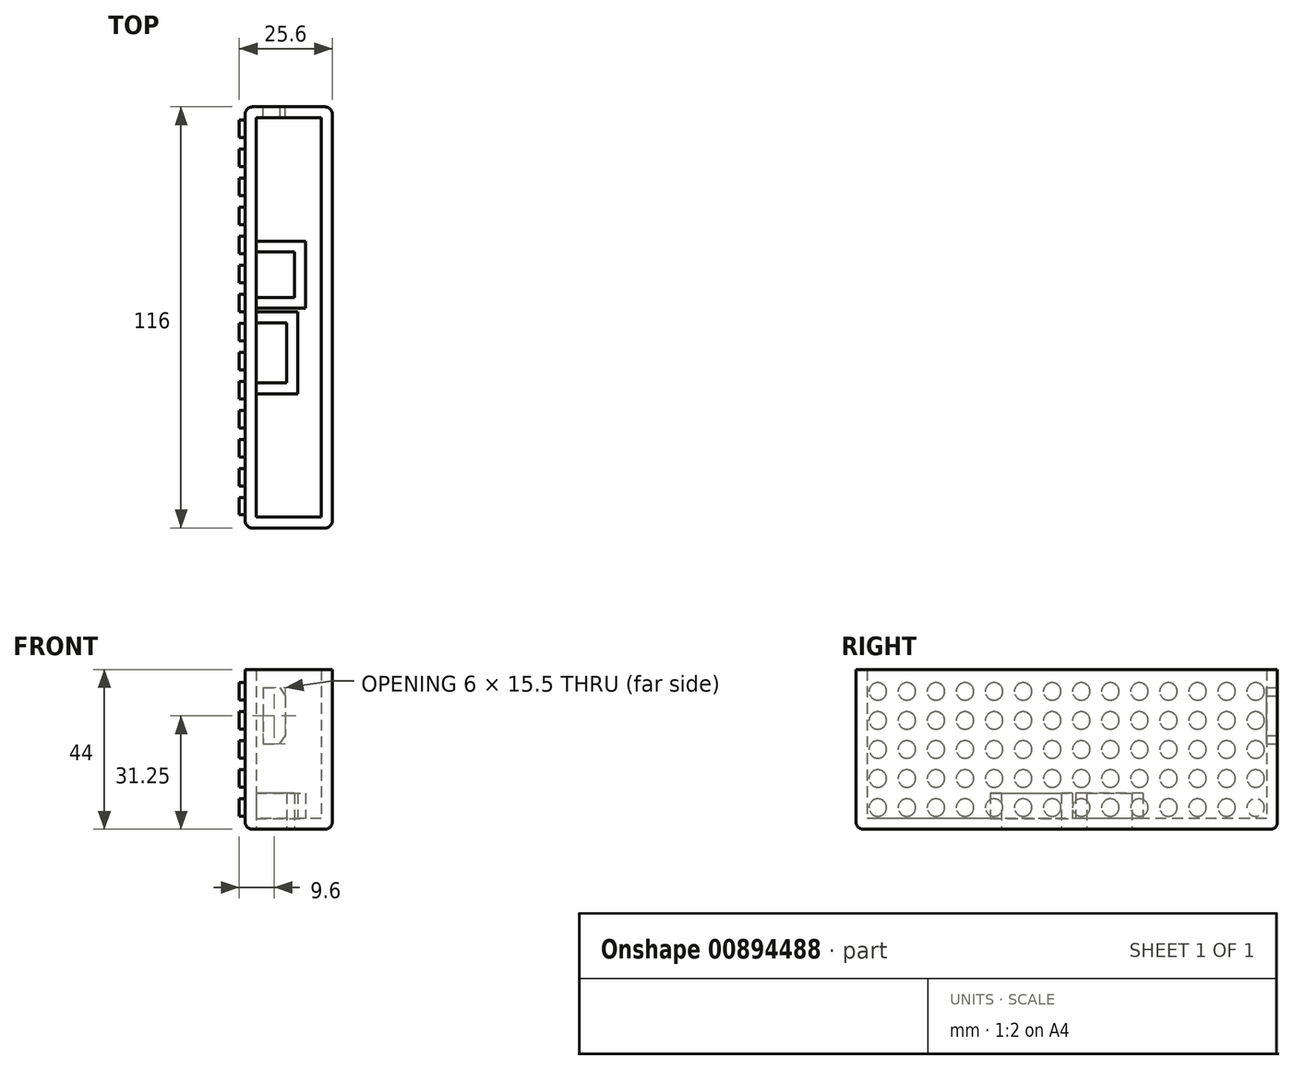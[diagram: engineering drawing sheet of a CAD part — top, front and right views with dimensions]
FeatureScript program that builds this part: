
annotation { "Feature Type Name" : "Feature", "Feature Type Description" : "" }
export const myFeature = defineFeature(function(context is Context, id is Id, definition is map)
    precondition{}
    {
        {
            var Q0;
            Q0=qCreatedBy(makeId("Top.planeOp"),FACE);
            var sketch = newSketch(context, id + "F0", { "sketchPlane" : qUnion([Q0])});
            skLineSegment(sketch, "E0.bottom", {"start": v(12, 58) * mm, "end": v(-12, 58) * mm});
            skLineSegment(sketch, "E0.top", {"start": v(12, -58) * mm, "end": v(-12, -58) * mm});
            skLineSegment(sketch, "E0.left", {"start": v(12, 58) * mm, "end": v(12, -58) * mm});
            skLineSegment(sketch, "E0.right", {"start": v(-12, 58) * mm, "end": v(-12, -58) * mm});
            skPoint(sketch, "E0.middle", {"position": v(0, 0) * mm});
            skSolve(sketch);
        }
        {
            var Q0;
            Q0=makeQuery(id+"F0.imprint","IMPRINT",FACE,{"disambiguationData":[TD([[makeQuery(id+"F0.imprint","IMPRINT",EDGE,{"derivedFrom":sQuery(id+"F0.wireOp",EDGE,"E0.bottom")}),1.0]])]});
            extrude(context, id + "F1", {"entities" : qUnion([Q0]), "depth" : 44 * mm, "offsetDistance" : 25 * mm});
        }
        {
            var Q0;
            Q0=makeQuery(id+"F1.opExtrude","CAP_FACE",FACE,{"disambiguationData":[OSD([sQuery(id+"F0.wireOp",EDGE,"E0.bottom"),sQuery(id+"F0.wireOp",EDGE,"E0.top"),sQuery(id+"F0.wireOp",EDGE,"E0.left"),sQuery(id+"F0.wireOp",EDGE,"E0.right")])],"isStart":false});
            shell(context, id + "F2", {"entities" : qUnion([Q0]), "thickness" : 3 * mm});
        }
        {
            var Q0;
            Q0=makeQuery(id+"F1.opExtrude","CAP_FACE",FACE,{"disambiguationData":[OSD([sQuery(id+"F0.wireOp",EDGE,"E0.bottom"),sQuery(id+"F0.wireOp",EDGE,"E0.top"),sQuery(id+"F0.wireOp",EDGE,"E0.left"),sQuery(id+"F0.wireOp",EDGE,"E0.right")])],"isStart":true});
            var sketch = newSketch(context, id + "F3", { "sketchPlane" : qUnion([Q0])});
            skLineSegment(sketch, "E1.bottom", {"start": v(-9, 1.5) * mm, "end": v(-0.5, 1.5) * mm});
            skLineSegment(sketch, "E1.top", {"start": v(-9, 18) * mm, "end": v(-0.5, 18) * mm});
            skLineSegment(sketch, "E1.left", {"start": v(-9, 1.5) * mm, "end": v(-9, 18) * mm});
            skLineSegment(sketch, "E1.right", {"start": v(-0.5, 1.5) * mm, "end": v(-0.5, 18) * mm});
            skLineSegment(sketch, "E2.bottom", {"start": v(-9, -18) * mm, "end": v(1.6, -18) * mm});
            skLineSegment(sketch, "E2.top", {"start": v(-9, -5.5) * mm, "end": v(1.6, -5.5) * mm});
            skLineSegment(sketch, "E2.left", {"start": v(-9, -18) * mm, "end": v(-9, -5.5) * mm});
            skLineSegment(sketch, "E2.right", {"start": v(1.6, -18) * mm, "end": v(1.6, -5.5) * mm});
            skSolve(sketch);
        }
        {
            var Q0;
            Q0 = qSketchRegion(id + "F3", true);
            extrude(context, id + "F4", {"entities" : qUnion([Q0]), "operationType" : NewBodyOperationType.REMOVE, "oppositeDirection" : true, "depth" : 25 * mm, "offsetDistance" : 25 * mm});
        }
        {
            var Q0;
            Q0=makeQuery(id+"F1.opExtrude","SWEPT_FACE",FACE,{"disambiguationData":[OSD([sQuery(id+"F0.wireOp",EDGE,"E0.bottom")])]});
            var sketch = newSketch(context, id + "F5", { "sketchPlane" : qUnion([Q0])});
            skLineSegment(sketch, "E3.bottom", {"start": v(7, 39) * mm, "end": v(1, 39) * mm});
            skLineSegment(sketch, "E3.top", {"start": v(7, 23.5) * mm, "end": v(1, 23.5) * mm});
            skLineSegment(sketch, "E3.left", {"start": v(7, 39) * mm, "end": v(7, 23.5) * mm});
            skLineSegment(sketch, "E3.right", {"start": v(1, 39) * mm, "end": v(1, 23.5) * mm});
            skSolve(sketch);
        }
        {
            var Q0;
            Q0 = qSketchRegion(id + "F5", true);
            extrude(context, id + "F6", {"entities" : qUnion([Q0]), "operationType" : NewBodyOperationType.REMOVE, "oppositeDirection" : true, "depth" : 25 * mm, "offsetDistance" : 25 * mm});
        }
        {
            var Q0;
            Q0=makeQuery(id+"F6.boolean.opBoolean","COPY",EDGE,{"derivedFrom":makeQuery(id+"F6.opExtrude","SWEPT_EDGE",EDGE,{"disambiguationData":[OSD([sQuery(id+"F5.wireOp",EDGE,"E3.top"),sQuery(id+"F5.wireOp",EDGE,"E3.right")])]})});
            var Q1;
            Q1=makeQuery(id+"F6.boolean.opBoolean","COPY",EDGE,{"derivedFrom":makeQuery(id+"F6.opExtrude","SWEPT_EDGE",EDGE,{"disambiguationData":[OSD([sQuery(id+"F5.wireOp",EDGE,"E3.bottom"),sQuery(id+"F5.wireOp",EDGE,"E3.right")])]})});
            chamfer(context, id + "F7", {"entities" : qUnion([Q0, Q1]), "chamferType" : ChamferType.TWO_OFFSETS, "width1" : 1.5 * mm, "oppositeDirection" : false, "width2" : 2.25 * mm, "tangentPropagation" : true});
        }
        {
            var Q0;
            Q0=makeQuery(id+"F2.opShell","OFFSET_FACE",FACE,{"disambiguationData":[OSD([sQuery(id+"F0.wireOp",EDGE,"E0.bottom"),sQuery(id+"F0.wireOp",EDGE,"E0.top"),sQuery(id+"F0.wireOp",EDGE,"E0.left"),sQuery(id+"F0.wireOp",EDGE,"E0.right")])]});
            var sketch = newSketch(context, id + "F8", { "sketchPlane" : qUnion([Q0])});
            skLineSegment(sketch, "E4.bottom", {"start": v(-9, 55) * mm, "end": v(9, 55) * mm});
            skLineSegment(sketch, "E4.top", {"start": v(-9, -55) * mm, "end": v(9, -55) * mm});
            skLineSegment(sketch, "E4.left", {"start": v(-9, 55) * mm, "end": v(-9, -55) * mm});
            skLineSegment(sketch, "E4.right", {"start": v(9, 55) * mm, "end": v(9, -55) * mm});
            skLineSegment(sketch, "E5.bottom", {"start": v(-9, 21) * mm, "end": v(4.6, 21) * mm});
            skLineSegment(sketch, "E5.top", {"start": v(-9, 2.5) * mm, "end": v(4.6, 2.5) * mm});
            skLineSegment(sketch, "E5.left", {"start": v(-9, 21) * mm, "end": v(-9, 2.5) * mm});
            skLineSegment(sketch, "E5.right", {"start": v(4.6, 21) * mm, "end": v(4.6, 2.5) * mm});
            skLineSegment(sketch, "E6.bottom", {"start": v(-9, -21) * mm, "end": v(2.5, -21) * mm});
            skLineSegment(sketch, "E6.top", {"start": v(-9, 1.5) * mm, "end": v(2.5, 1.5) * mm});
            skLineSegment(sketch, "E6.left", {"start": v(-9, -21) * mm, "end": v(-9, 1.5) * mm});
            skLineSegment(sketch, "E6.right", {"start": v(2.5, -21) * mm, "end": v(2.5, 1.5) * mm});
            skSolve(sketch);
        }
        {
            var Q0;
            {var subQ6=sQuery(id+"F8.wireOp",EDGE,"E5.bottom");Q0=makeQuery(id+"F8.imprint","IMPRINT",FACE,{"disambiguationData":[TD([[makeQuery(id+"F8.imprint","IMPRINT",EDGE,{"derivedFrom":subQ6}),-1.0]])]});}
            var Q1;
            {var subQ3=sQuery(id+"F8.wireOp",EDGE,"E6.bottom");Q1=makeQuery(id+"F8.imprint","IMPRINT",FACE,{"disambiguationData":[TD([[makeQuery(id+"F8.imprint","IMPRINT",EDGE,{"derivedFrom":subQ3}),1.0]])]});}
            extrude(context, id + "F9", {"entities" : qUnion([Q0, Q1]), "operationType" : NewBodyOperationType.ADD, "depth" : 7 * mm, "offsetDistance" : 25 * mm});
        }
        {
            var Q0;
            Q0=makeQuery(id+"F1.opExtrude","SWEPT_FACE",FACE,{"disambiguationData":[OSD([sQuery(id+"F0.wireOp",EDGE,"E0.right")])]});
            var sketch = newSketch(context, id + "F10", { "sketchPlane" : qUnion([Q0])});
            skCircle(sketch, "E7", {"center": v(-52, 6) * mm, "radius": 2.4 * mm});
            skCircle(sketch, "E8.0.1.0", {"center": v(-52, 14) * mm, "radius": 2.4 * mm});
            skCircle(sketch, "E8.0.2.0", {"center": v(-52, 22) * mm, "radius": 2.4 * mm});
            skCircle(sketch, "E8.0.3.0", {"center": v(-52, 30) * mm, "radius": 2.4 * mm});
            skCircle(sketch, "E8.0.4.0", {"center": v(-52, 38) * mm, "radius": 2.4 * mm});
            skCircle(sketch, "E8.1.0.0", {"center": v(-44, 6) * mm, "radius": 2.4 * mm});
            skCircle(sketch, "E8.1.1.0", {"center": v(-44, 14) * mm, "radius": 2.4 * mm});
            skCircle(sketch, "E8.1.2.0", {"center": v(-44, 22) * mm, "radius": 2.4 * mm});
            skCircle(sketch, "E8.1.3.0", {"center": v(-44, 30) * mm, "radius": 2.4 * mm});
            skCircle(sketch, "E8.1.4.0", {"center": v(-44, 38) * mm, "radius": 2.4 * mm});
            skCircle(sketch, "E8.2.0.0", {"center": v(-36, 6) * mm, "radius": 2.4 * mm});
            skCircle(sketch, "E8.2.1.0", {"center": v(-36, 14) * mm, "radius": 2.4 * mm});
            skCircle(sketch, "E8.2.2.0", {"center": v(-36, 22) * mm, "radius": 2.4 * mm});
            skCircle(sketch, "E8.2.3.0", {"center": v(-36, 30) * mm, "radius": 2.4 * mm});
            skCircle(sketch, "E8.2.4.0", {"center": v(-36, 38) * mm, "radius": 2.4 * mm});
            skCircle(sketch, "E8.3.0.0", {"center": v(-28, 6) * mm, "radius": 2.4 * mm});
            skCircle(sketch, "E8.3.1.0", {"center": v(-28, 14) * mm, "radius": 2.4 * mm});
            skCircle(sketch, "E8.3.2.0", {"center": v(-28, 22) * mm, "radius": 2.4 * mm});
            skCircle(sketch, "E8.3.3.0", {"center": v(-28, 30) * mm, "radius": 2.4 * mm});
            skCircle(sketch, "E8.3.4.0", {"center": v(-28, 38) * mm, "radius": 2.4 * mm});
            skCircle(sketch, "E8.4.0.0", {"center": v(-20, 6) * mm, "radius": 2.4 * mm});
            skCircle(sketch, "E8.4.1.0", {"center": v(-20, 14) * mm, "radius": 2.4 * mm});
            skCircle(sketch, "E8.4.2.0", {"center": v(-20, 22) * mm, "radius": 2.4 * mm});
            skCircle(sketch, "E8.4.3.0", {"center": v(-20, 30) * mm, "radius": 2.4 * mm});
            skCircle(sketch, "E8.4.4.0", {"center": v(-20, 38) * mm, "radius": 2.4 * mm});
            skCircle(sketch, "E8.5.0.0", {"center": v(-12, 6) * mm, "radius": 2.4 * mm});
            skCircle(sketch, "E8.5.1.0", {"center": v(-12, 14) * mm, "radius": 2.4 * mm});
            skCircle(sketch, "E8.5.2.0", {"center": v(-12, 22) * mm, "radius": 2.4 * mm});
            skCircle(sketch, "E8.5.3.0", {"center": v(-12, 30) * mm, "radius": 2.4 * mm});
            skCircle(sketch, "E8.5.4.0", {"center": v(-12, 38) * mm, "radius": 2.4 * mm});
            skCircle(sketch, "E8.6.0.0", {"center": v(-4, 6) * mm, "radius": 2.4 * mm});
            skCircle(sketch, "E8.6.1.0", {"center": v(-4, 14) * mm, "radius": 2.4 * mm});
            skCircle(sketch, "E8.6.2.0", {"center": v(-4, 22) * mm, "radius": 2.4 * mm});
            skCircle(sketch, "E8.6.3.0", {"center": v(-4, 30) * mm, "radius": 2.4 * mm});
            skCircle(sketch, "E8.6.4.0", {"center": v(-4, 38) * mm, "radius": 2.4 * mm});
            skCircle(sketch, "E8.7.0.0", {"center": v(4, 6) * mm, "radius": 2.4 * mm});
            skCircle(sketch, "E8.7.1.0", {"center": v(4, 14) * mm, "radius": 2.4 * mm});
            skCircle(sketch, "E8.7.2.0", {"center": v(4, 22) * mm, "radius": 2.4 * mm});
            skCircle(sketch, "E8.7.3.0", {"center": v(4, 30) * mm, "radius": 2.4 * mm});
            skCircle(sketch, "E8.7.4.0", {"center": v(4, 38) * mm, "radius": 2.4 * mm});
            skCircle(sketch, "E8.8.0.0", {"center": v(12, 6) * mm, "radius": 2.4 * mm});
            skCircle(sketch, "E8.8.1.0", {"center": v(12, 14) * mm, "radius": 2.4 * mm});
            skCircle(sketch, "E8.8.2.0", {"center": v(12, 22) * mm, "radius": 2.4 * mm});
            skCircle(sketch, "E8.8.3.0", {"center": v(12, 30) * mm, "radius": 2.4 * mm});
            skCircle(sketch, "E8.8.4.0", {"center": v(12, 38) * mm, "radius": 2.4 * mm});
            skCircle(sketch, "E8.9.0.0", {"center": v(20, 6) * mm, "radius": 2.4 * mm});
            skCircle(sketch, "E8.9.1.0", {"center": v(20, 14) * mm, "radius": 2.4 * mm});
            skCircle(sketch, "E8.9.2.0", {"center": v(20, 22) * mm, "radius": 2.4 * mm});
            skCircle(sketch, "E8.9.3.0", {"center": v(20, 30) * mm, "radius": 2.4 * mm});
            skCircle(sketch, "E8.9.4.0", {"center": v(20, 38) * mm, "radius": 2.4 * mm});
            skCircle(sketch, "E8.10.0.0", {"center": v(28, 6) * mm, "radius": 2.4 * mm});
            skCircle(sketch, "E8.10.1.0", {"center": v(28, 14) * mm, "radius": 2.4 * mm});
            skCircle(sketch, "E8.10.2.0", {"center": v(28, 22) * mm, "radius": 2.4 * mm});
            skCircle(sketch, "E8.10.3.0", {"center": v(28, 30) * mm, "radius": 2.4 * mm});
            skCircle(sketch, "E8.10.4.0", {"center": v(28, 38) * mm, "radius": 2.4 * mm});
            skCircle(sketch, "E8.11.0.0", {"center": v(36, 6) * mm, "radius": 2.4 * mm});
            skCircle(sketch, "E8.11.1.0", {"center": v(36, 14) * mm, "radius": 2.4 * mm});
            skCircle(sketch, "E8.11.2.0", {"center": v(36, 22) * mm, "radius": 2.4 * mm});
            skCircle(sketch, "E8.11.3.0", {"center": v(36, 30) * mm, "radius": 2.4 * mm});
            skCircle(sketch, "E8.11.4.0", {"center": v(36, 38) * mm, "radius": 2.4 * mm});
            skCircle(sketch, "E8.12.0.0", {"center": v(44, 6) * mm, "radius": 2.4 * mm});
            skCircle(sketch, "E8.12.1.0", {"center": v(44, 14) * mm, "radius": 2.4 * mm});
            skCircle(sketch, "E8.12.2.0", {"center": v(44, 22) * mm, "radius": 2.4 * mm});
            skCircle(sketch, "E8.12.3.0", {"center": v(44, 30) * mm, "radius": 2.4 * mm});
            skCircle(sketch, "E8.12.4.0", {"center": v(44, 38) * mm, "radius": 2.4 * mm});
            skCircle(sketch, "E8.13.0.0", {"center": v(52, 6) * mm, "radius": 2.4 * mm});
            skCircle(sketch, "E8.13.1.0", {"center": v(52, 14) * mm, "radius": 2.4 * mm});
            skCircle(sketch, "E8.13.2.0", {"center": v(52, 22) * mm, "radius": 2.4 * mm});
            skCircle(sketch, "E8.13.3.0", {"center": v(52, 30) * mm, "radius": 2.4 * mm});
            skCircle(sketch, "E8.13.4.0", {"center": v(52, 38) * mm, "radius": 2.4 * mm});
            skLineSegment(sketch, "E8.direction1", {"start": v(-52, 6) * mm, "end": v(-44, 6) * mm, "construction": true});
            skLineSegment(sketch, "E8.direction2", {"start": v(-52, 6) * mm, "end": v(-52, 14) * mm, "construction": true});
            skSolve(sketch);
        }
        {
            var Q0;
            Q0 = qSketchRegion(id + "F10", true);
            extrude(context, id + "F11", {"entities" : qUnion([Q0]), "operationType" : NewBodyOperationType.ADD, "depth" : 1.6 * mm, "offsetDistance" : 25 * mm});
        }
        {
            var Q0;
            Q0=makeQuery(id+"F1.opExtrude","CAP_EDGE",EDGE,{"disambiguationData":[OSD([sQuery(id+"F0.wireOp",EDGE,"E0.left")])],"isStart":true});
            var Q1;
            Q1=makeQuery(id+"F1.opExtrude","CAP_EDGE",EDGE,{"disambiguationData":[OSD([sQuery(id+"F0.wireOp",EDGE,"E0.top")])],"isStart":true});
            var Q2;
            Q2=makeQuery(id+"F1.opExtrude","CAP_EDGE",EDGE,{"disambiguationData":[OSD([sQuery(id+"F0.wireOp",EDGE,"E0.right")])],"isStart":true});
            var Q3;
            Q3=makeQuery(id+"F1.opExtrude","CAP_EDGE",EDGE,{"disambiguationData":[OSD([sQuery(id+"F0.wireOp",EDGE,"E0.bottom")])],"isStart":true});
            fillet(context, id + "F12", {"entities" : qUnion([Q0, Q1, Q2, Q3]), "radius" : 2 * mm, "tangentPropagation" : true, "allowEdgeOverflow" : false});
        }
        {
            var Q0;
            Q0=makeQuery(id+"F1.opExtrude","SWEPT_EDGE",EDGE,{"disambiguationData":[OSD([sQuery(id+"F0.wireOp",EDGE,"E0.top"),sQuery(id+"F0.wireOp",EDGE,"E0.right")])]});
            var Q1;
            Q1=makeQuery(id+"F1.opExtrude","SWEPT_EDGE",EDGE,{"disambiguationData":[OSD([sQuery(id+"F0.wireOp",EDGE,"E0.top"),sQuery(id+"F0.wireOp",EDGE,"E0.left")])]});
            var Q2;
            Q2=makeQuery(id+"F1.opExtrude","SWEPT_EDGE",EDGE,{"disambiguationData":[OSD([sQuery(id+"F0.wireOp",EDGE,"E0.bottom"),sQuery(id+"F0.wireOp",EDGE,"E0.left")])]});
            var Q3;
            Q3=makeQuery(id+"F1.opExtrude","SWEPT_EDGE",EDGE,{"disambiguationData":[OSD([sQuery(id+"F0.wireOp",EDGE,"E0.bottom"),sQuery(id+"F0.wireOp",EDGE,"E0.right")])]});
            fillet(context, id + "F13", {"entities" : qUnion([Q0, Q1, Q2, Q3]), "radius" : 2 * mm, "tangentPropagation" : true, "allowEdgeOverflow" : false});
        }
    });
